# Revit family: ERA_LF_CR_SPO-7-40
name_source: partatom
category: Осветительные приборы
units: mm (PartAtom-declared; Revit-internal decimal feet)

## family parameters
Всегда вертикально = Да
Заголовок OmniClass = Lighting
Источник света = Да
На основе рабочей плоскости = Нет
Номер OmniClass = 23.80.70.00
Общий = Нет
При загрузке вырезать с полостями = Нет
Размер круглого соединителя = Использовать диаметр
Тип детали = Нормальный
Точка расчета площади = Да

## types (4) — shared parameters
ADSK_Единица измерения = шт.
ADSK_Завод-изготовитель = ЭРА
ADSK_Классификация нагрузок = Освещение
ADSK_Количество фаз = 1
ADSK_Коэффициент мощности = 0.9
ADSK_Наименование краткое = Светильник
ADSK_Напряжение = 230 В
ADSK_Номинальная мощность = 40 Вт
ADSK_Полная мощность = 44 В·А
ADSK_Примечание = Импульсный драйвер, поликарбонат
ADSK_Размер_Высота = 19 мм
ADSK_Размер_Длина = 1200 мм
ADSK_Размер_Ширина = 180 мм
URL = https://www.eraworld.ru
_Корпус_Высота = 19 мм
_Корпус_Диаметр = 1 мм
_Корпус_Длина = 1200 мм
_Корпус_Ширина = 180 мм
_УГО_Диаметр = 12 мм
_УГО_Длина = 12 мм
_УГО_Ширина = 1.8 мм
Видимая форма излучения при визуализации = Нет
Геометрия изделия = Прямоугольный
Излучение по длине прямоугольника = 1200 мм
Излучение по ширине прямоугольника = 180 мм
Источник света = LED
Класс защиты = I
Класс пожароопасности = Нет
Комплект = Импульсный драйвер, поликарбонат
Разработчик модели = https://www.teslabim.ru
Светофильтр = 16777215
Смещение цветовой температуры при затухании лампы = <Нет>
Степень защиты IP = IP40
Тип установки = Потолочный
УГО_Масштаб = 100
Угол наклона = 90,00°
Цвет = Белый
zero-valued in all types: ADSK_Размер_Диаметр

## per-type parameters (varying)
| type | ADSK_Марка | ADSK_Масса | ADSK_Наименование | ADSK_Обозначение | Файл фотометрической сетки |
| SPO-7-40-6K-P, LED, IP40, 1200х180х19 мм (ДхШхВ), 40 Вт, 6500 К, 2800 лм, класс защиты I, в комплекте (импульсный драйвер, поликарбонат) | SPO-7-40-6K-P | 1.08 | Светильник, LED, прямоугольный, потолочный, IP40, 1200х180х19 мм (ДхШхВ), 40 Вт, 6500 К, 2800 лм, класс защиты I, в комплекте (импульсный драйвер, поликарбонат) | SPO-7-40-6K-P | SPO-7-40-6K-P.ies |
| SPO-7-40-4K-P, LED, IP40, 1200х180х19 мм (ДхШхВ), 40 Вт, 4000 К, 2800 лм, класс защиты I, в комплекте (импульсный драйвер, поликарбонат) | SPO-7-40-4K-P | 1.08 | Светильник, LED, прямоугольный, потолочный, IP40, 1200х180х19 мм (ДхШхВ), 40 Вт, 4000 К, 2800 лм, класс защиты I, в комплекте (импульсный драйвер, поликарбонат) | SPO-7-40-4K-P | SPO-7-40-4K-P.ies |
| SPO-7-40-6K-M, LED, IP40, 1200х180х19 мм (ДхШхВ), 40 Вт, 6500 К, 2800 лм, класс защиты I, в комплекте (импульсный драйвер, поликарбонат) | SPO-7-40-6K-M | 1.1 | Светильник, LED, прямоугольный, потолочный, IP40, 1200х180х19 мм (ДхШхВ), 40 Вт, 6500 К, 2800 лм, класс защиты I, в комплекте (импульсный драйвер, поликарбонат) | SPO-7-40-6K-M | SPO-7-40-6K-M.ies |
| SPO-7-40-4K-M, LED, IP40, 1200х180х19 мм (ДхШхВ), 40 Вт, 4000 К, 2800 лм, класс защиты I, в комплекте (импульсный драйвер, поликарбонат) | SPO-7-40-4K-M | 1.08 | Светильник, LED, прямоугольный, потолочный, IP40, 1200х180х19 мм (ДхШхВ), 40 Вт, 4000 К, 2800 лм, класс защиты I, в комплекте (импульсный драйвер, поликарбонат) | SPO-7-40-4K-M | SPO-7-40-4K-M.ies |
